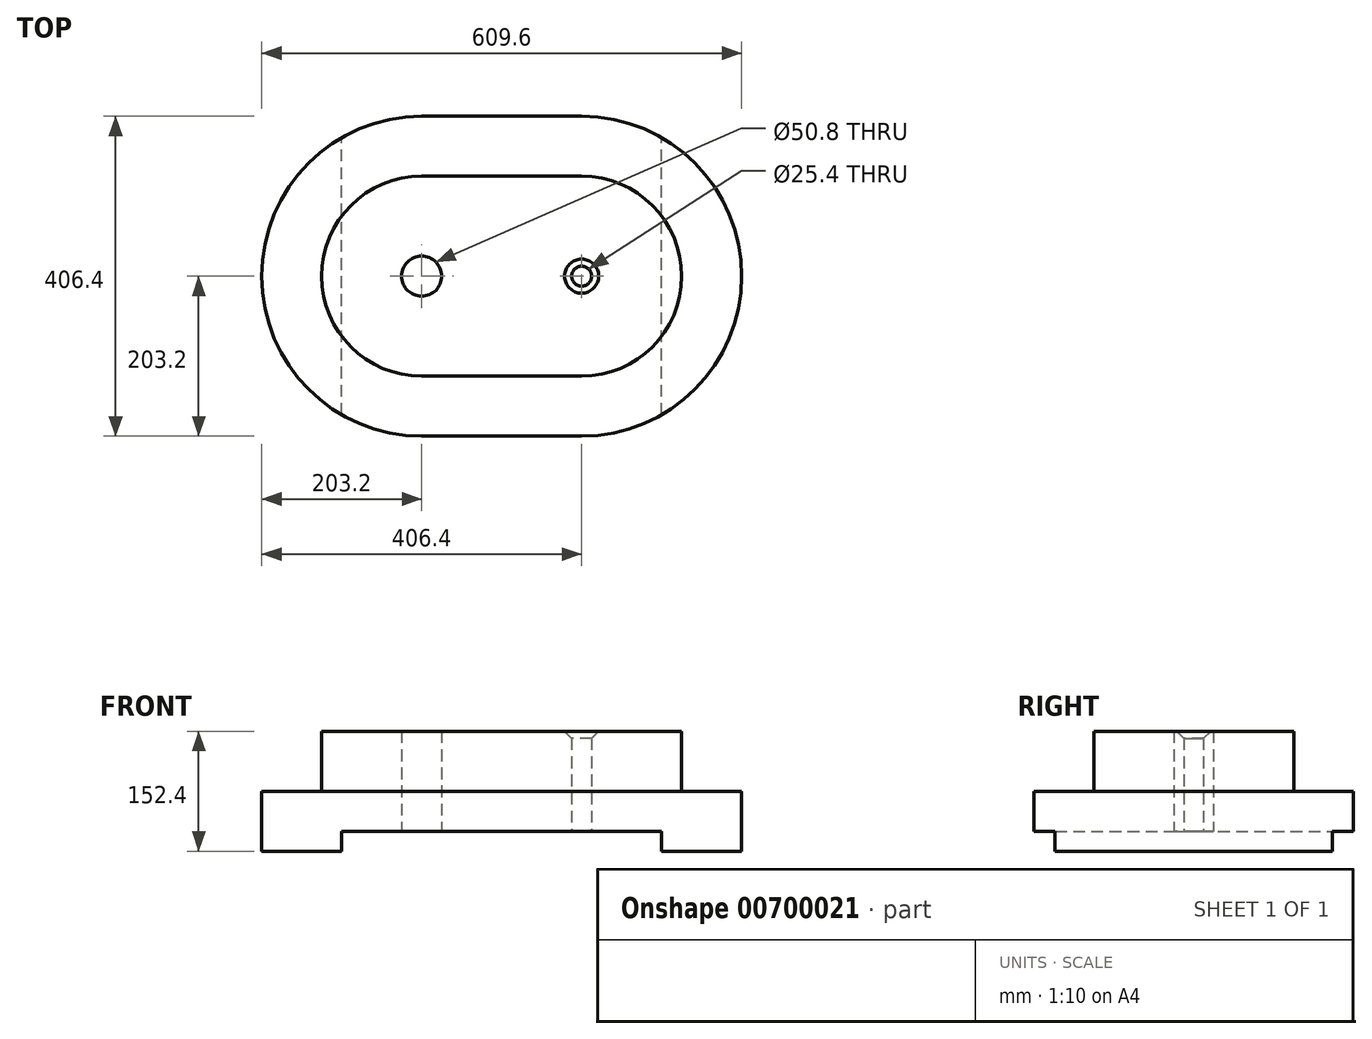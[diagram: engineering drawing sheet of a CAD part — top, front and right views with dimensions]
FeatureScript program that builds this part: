
annotation { "Feature Type Name" : "Feature", "Feature Type Description" : "" }
export const myFeature = defineFeature(function(context is Context, id is Id, definition is map)
    precondition{}
    {
        {
            var Q0;
            Q0=qCreatedBy(makeId("Top.planeOp"),FACE);
            var sketch = newSketch(context, id + "F0", { "sketchPlane" : qUnion([Q0])});
            skArc(sketch, "E0", {"start": v(-101.6, 0) * mm, "mid": v(-304.8, -203.2) * mm, "end": v(-101.6, -406.4) * mm});
            skLineSegment(sketch, "E1", {"start": v(-101.6, 0) * mm, "end": v(101.6, 0) * mm});
            skLineSegment(sketch, "E2", {"start": v(-101.6, -406.4) * mm, "end": v(101.6, -406.4) * mm});
            skArc(sketch, "E3.trimOffspring", {"start": v(101.6, -406.4) * mm, "mid": v(304.8, -203.2) * mm, "end": v(101.6, 0) * mm});
            skCircle(sketch, "E4", {"center": v(101.6, -203.2) * mm, "radius": 12.7 * mm});
            skCircle(sketch, "E5", {"center": v(101.6, -203.2) * mm, "radius": 25.4 * mm});
            skCircle(sketch, "E6", {"center": v(101.6, -203.2) * mm, "radius": 50.8 * mm});
            skArc(sketch, "E7", {"start": v(101.6, -273.05) * mm, "mid": v(171.45, -203.2) * mm, "end": v(101.6, -133.35) * mm});
            skArc(sketch, "E8.MirrorC", {"start": v(-101.6, -273.05) * mm, "mid": v(-171.45, -203.2) * mm, "end": v(-101.6, -133.35) * mm});
            skCircle(sketch, "E9.MirrorC", {"center": v(-101.6, -203.2) * mm, "radius": 50.8 * mm});
            skCircle(sketch, "E10.MirrorC", {"center": v(-101.6, -203.2) * mm, "radius": 25.4 * mm});
            skCircle(sketch, "E11.MirrorC", {"center": v(-101.6, -203.2) * mm, "radius": 12.7 * mm});
            skLineSegment(sketch, "E12", {"start": v(-101.6, -76.2) * mm, "end": v(101.6, -76.2) * mm});
            skLineSegment(sketch, "E13", {"start": v(-101.6, -330.2) * mm, "end": v(101.6, -330.2) * mm});
            skLineSegment(sketch, "E14", {"start": v(-101.6, -133.35) * mm, "end": v(101.6, -133.35) * mm});
            skLineSegment(sketch, "E15", {"start": v(101.6, -330.2) * mm, "end": v(-101.6, -330.2) * mm});
            skLineSegment(sketch, "E16", {"start": v(-101.6, -273.05) * mm, "end": v(101.6, -273.05) * mm});
            skArc(sketch, "E17.trimOffspring", {"start": v(-101.6, -330.2) * mm, "mid": v(-228.6, -203.2) * mm, "end": v(-101.6, -76.2) * mm});
            skArc(sketch, "E18.trimOffspring", {"start": v(101.6, -330.2) * mm, "mid": v(228.6, -203.2) * mm, "end": v(101.6, -76.2) * mm});
            skSolve(sketch);
        }
        {
            var Q0;
            Q0=qCreatedBy(makeId("Front.planeOp"),FACE);
            var sketch = newSketch(context, id + "F1", { "sketchPlane" : qUnion([Q0])});
            skLineSegment(sketch, "E19.bottom", {"start": v(-203.2, 0) * mm, "end": v(203.2, 0) * mm});
            skLineSegment(sketch, "E19.top", {"start": v(-203.2, 25.4) * mm, "end": v(203.2, 25.4) * mm});
            skLineSegment(sketch, "E19.left", {"start": v(-203.2, 0) * mm, "end": v(-203.2, 25.4) * mm});
            skLineSegment(sketch, "E19.right", {"start": v(203.2, 0) * mm, "end": v(203.2, 25.4) * mm});
            skSolve(sketch);
        }
        {
            var Q0;
            Q0=makeQuery(id+"F0.imprint","IMPRINT",FACE,{"disambiguationData":[TD([[makeQuery(id+"F0.imprint","IMPRINT",EDGE,{"derivedFrom":sQuery(id+"F0.wireOp",EDGE,"E4")}),-1.0]])]});
            var Q1;
            Q1=makeQuery(id+"F0.imprint","IMPRINT",FACE,{"disambiguationData":[TD([[makeQuery(id+"F0.imprint","IMPRINT",EDGE,{"derivedFrom":sQuery(id+"F0.wireOp",EDGE,"E5")}),-1.0]])]});
            var Q2;
            Q2=makeQuery(id+"F0.imprint","IMPRINT",FACE,{"disambiguationData":[TD([[makeQuery(id+"F0.imprint","IMPRINT",EDGE,{"derivedFrom":sQuery(id+"F0.wireOp",EDGE,"E4")}),1.0]])]});
            var Q3;
            Q3=makeQuery(id+"F0.imprint","IMPRINT",FACE,{"disambiguationData":[TD([[makeQuery(id+"F0.imprint","IMPRINT",EDGE,{"derivedFrom":sQuery(id+"F0.wireOp",EDGE,"E11.MirrorC")}),-1.0]])]});
            var Q4;
            Q4=makeQuery(id+"F0.imprint","IMPRINT",FACE,{"disambiguationData":[TD([[makeQuery(id+"F0.imprint","IMPRINT",EDGE,{"derivedFrom":sQuery(id+"F0.wireOp",EDGE,"E10.MirrorC")}),-1.0]])]});
            var Q5;
            Q5=makeQuery(id+"F0.imprint","IMPRINT",FACE,{"disambiguationData":[TD([[makeQuery(id+"F0.imprint","IMPRINT",EDGE,{"derivedFrom":sQuery(id+"F0.wireOp",EDGE,"E9.MirrorC")}),-1.0]])]});
            var Q6;
            Q6=makeQuery(id+"F0.imprint","IMPRINT",FACE,{"disambiguationData":[TD([[makeQuery(id+"F0.imprint","IMPRINT",EDGE,{"derivedFrom":sQuery(id+"F0.wireOp",EDGE,"E6")}),-1.0]])]});
            var Q7;
            Q7=makeQuery(id+"F0.imprint","IMPRINT",FACE,{"disambiguationData":[TD([[makeQuery(id+"F0.imprint","IMPRINT",EDGE,{"derivedFrom":sQuery(id+"F0.wireOp",EDGE,"E7")}),-1.0]])]});
            var Q8;
            Q8=makeQuery(id+"F0.imprint","IMPRINT",FACE,{"disambiguationData":[TD([[makeQuery(id+"F0.imprint","IMPRINT",EDGE,{"derivedFrom":sQuery(id+"F0.wireOp",EDGE,"E0")}),1.0]])]});
            extrude(context, id + "F2", {"entities" : qUnion([Q0, Q1, Q2, Q3, Q4, Q5, Q6, Q7, Q8]), "depth" : 76.2 * mm, "offsetDistance" : 25.4 * mm});
        }
        {
            var Q0;
            Q0=makeQuery(id+"F0.imprint","IMPRINT",FACE,{"disambiguationData":[TD([[makeQuery(id+"F0.imprint","IMPRINT",EDGE,{"derivedFrom":sQuery(id+"F0.wireOp",EDGE,"E7")}),-1.0]])]});
            var Q1;
            Q1=makeQuery(id+"F0.imprint","IMPRINT",FACE,{"disambiguationData":[TD([[makeQuery(id+"F0.imprint","IMPRINT",EDGE,{"derivedFrom":sQuery(id+"F0.wireOp",EDGE,"E5")}),-1.0]])]});
            var Q2;
            Q2=makeQuery(id+"F0.imprint","IMPRINT",FACE,{"disambiguationData":[TD([[makeQuery(id+"F0.imprint","IMPRINT",EDGE,{"derivedFrom":sQuery(id+"F0.wireOp",EDGE,"E4")}),-1.0]])]});
            var Q3;
            Q3=makeQuery(id+"F0.imprint","IMPRINT",FACE,{"disambiguationData":[TD([[makeQuery(id+"F0.imprint","IMPRINT",EDGE,{"derivedFrom":sQuery(id+"F0.wireOp",EDGE,"E4")}),1.0]])]});
            var Q4;
            Q4=makeQuery(id+"F0.imprint","IMPRINT",FACE,{"disambiguationData":[TD([[makeQuery(id+"F0.imprint","IMPRINT",EDGE,{"derivedFrom":sQuery(id+"F0.wireOp",EDGE,"E10.MirrorC")}),-1.0]])]});
            var Q5;
            Q5=makeQuery(id+"F0.imprint","IMPRINT",FACE,{"disambiguationData":[TD([[makeQuery(id+"F0.imprint","IMPRINT",EDGE,{"derivedFrom":sQuery(id+"F0.wireOp",EDGE,"E11.MirrorC")}),-1.0]])]});
            var Q6;
            Q6=makeQuery(id+"F0.imprint","IMPRINT",FACE,{"disambiguationData":[TD([[makeQuery(id+"F0.imprint","IMPRINT",EDGE,{"derivedFrom":sQuery(id+"F0.wireOp",EDGE,"E9.MirrorC")}),-1.0]])]});
            extrude(context, id + "F3", {"entities" : qUnion([Q0, Q1, Q2, Q3, Q4, Q5, Q6]), "operationType" : NewBodyOperationType.ADD, "depth" : 152.4 * mm, "offsetDistance" : 25.4 * mm});
        }
        {
            var Q0;
            Q0=makeQuery(id+"F0.imprint","IMPRINT",FACE,{"disambiguationData":[TD([[makeQuery(id+"F0.imprint","IMPRINT",EDGE,{"derivedFrom":sQuery(id+"F0.wireOp",EDGE,"E4")}),1.0]])]});
            var Q1;
            Q1=makeQuery(id+"F0.imprint","IMPRINT",FACE,{"disambiguationData":[TD([[makeQuery(id+"F0.imprint","IMPRINT",EDGE,{"derivedFrom":sQuery(id+"F0.wireOp",EDGE,"E11.MirrorC")}),-1.0]])]});
            extrude(context, id + "F4", {"entities" : qUnion([Q0, Q1]), "operationType" : NewBodyOperationType.REMOVE, "depth" : 281.18 * mm, "offsetDistance" : 25.4 * mm});
        }
        {
            var Q0;
            Q0=makeQuery(id+"F4.boolean.opBoolean","COPY",FACE,{"derivedFrom":makeQuery(id+"F4.opExtrude","SWEPT_FACE",FACE,{"disambiguationData":[OSD([sQuery(id+"F0.wireOp",EDGE,"E4")])]})});
            var Q1;
            Q1=makeQuery(id+"F4.boolean.opBoolean","COPY",FACE,{"derivedFrom":makeQuery(id+"F4.opExtrude","SWEPT_FACE",FACE,{"disambiguationData":[OSD([sQuery(id+"F0.wireOp",EDGE,"E11.MirrorC")])]})});
            chamfer(context, id + "F5", {"entities" : qUnion([Q0, Q1]), "width" : 8.9 * mm, "tangentPropagation" : true});
        }
        {
            var Q0;
            Q0 = qSketchRegion(id + "F1", true);
            extrude(context, id + "F6", {"entities" : qUnion([Q0]), "operationType" : NewBodyOperationType.REMOVE, "depth" : 715.52 * mm, "offsetDistance" : 25.4 * mm});
        }
    });
